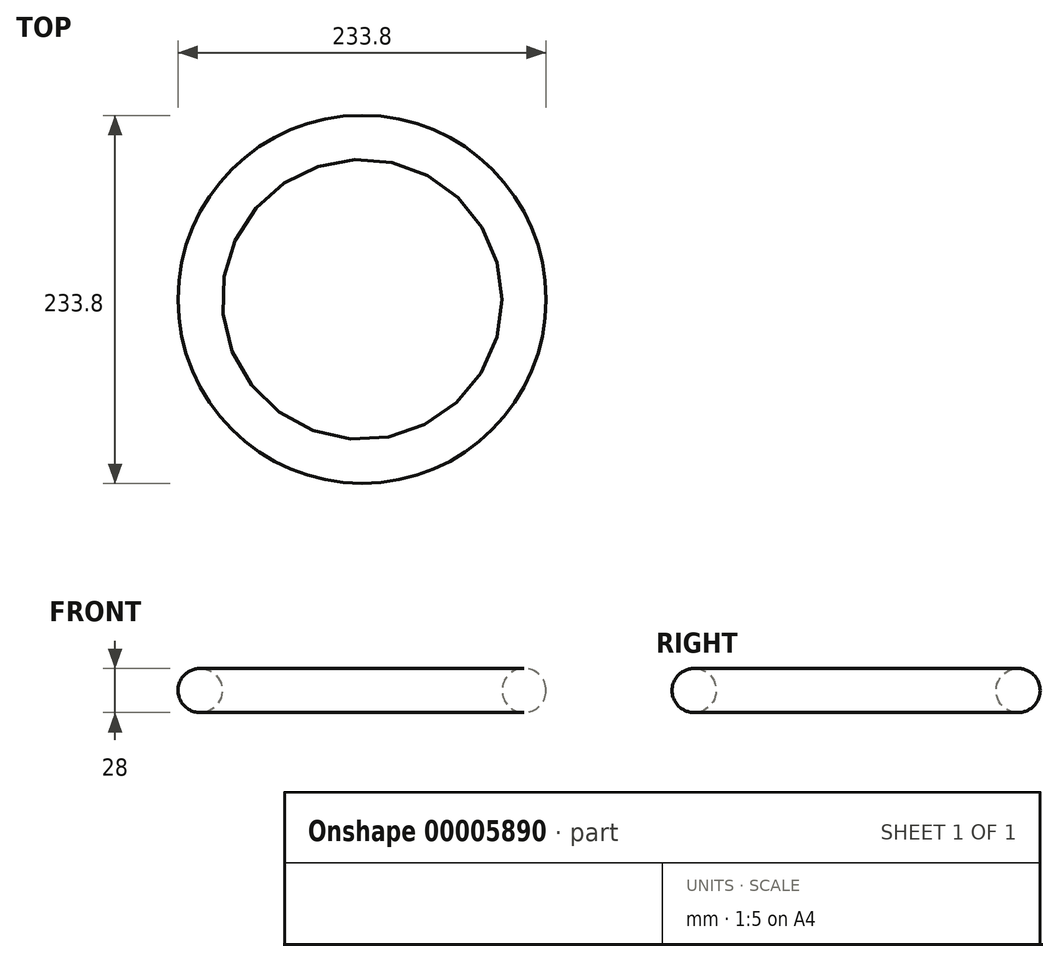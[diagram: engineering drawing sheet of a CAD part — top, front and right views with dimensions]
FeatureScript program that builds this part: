
annotation { "Feature Type Name" : "Feature", "Feature Type Description" : "" }
export const myFeature = defineFeature(function(context is Context, id is Id, definition is map)
    precondition{}
    {
        {
            var Q0;
            Q0=qCreatedBy(makeId("Right.planeOp"),FACE);
            var sketch = newSketch(context, id + "F0", { "sketchPlane" : qUnion([Q0])});
            skCircle(sketch, "E0", {"center": v(102.9, 0) * mm, "radius": 14 * mm});
            skLineSegment(sketch, "E1", {"start": v(0, 27.6) * mm, "end": v(0, -27.6) * mm, "construction": true});
            skPoint(sketch, "E2", {"position": v(88.9, 0) * mm});
            skSolve(sketch);
        }
        {
            var Q0;
            Q0 = qSketchRegion(id + "F0", true);
            var Q1;
            Q1=sQuery(id+"F0.wireOp",EDGE,"E1");
            revolve(context, id + "F1", {"entities" : qUnion([Q0]), "axis" : qUnion([Q1]), "revolveType" : RevolveType.FULL});
        }
    });
